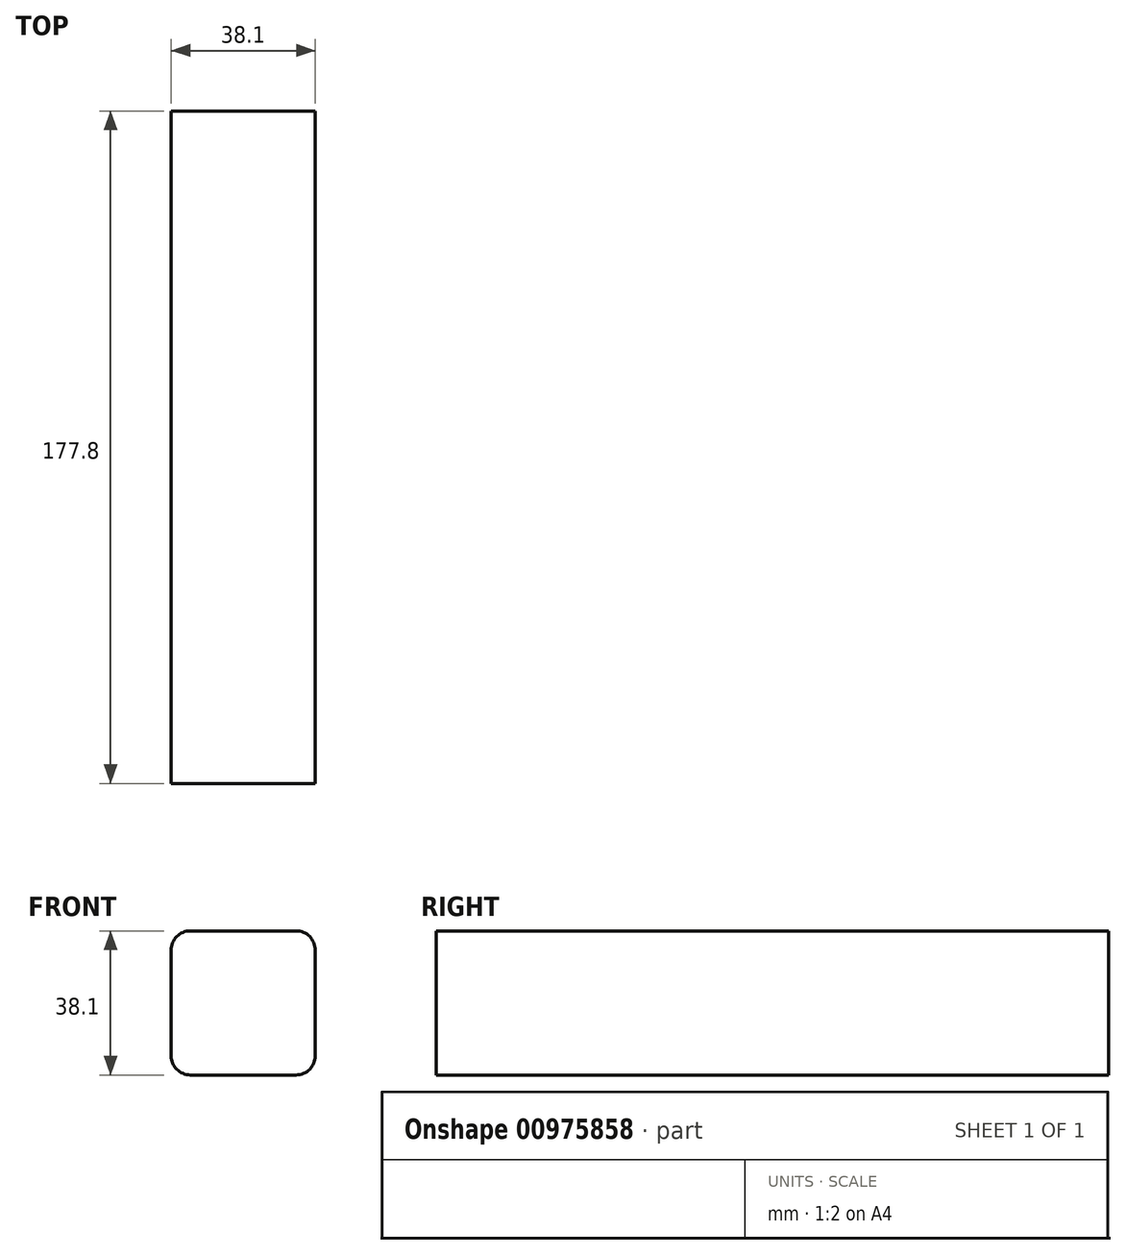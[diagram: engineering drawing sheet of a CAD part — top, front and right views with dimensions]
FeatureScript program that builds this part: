
annotation { "Feature Type Name" : "Feature", "Feature Type Description" : "" }
export const myFeature = defineFeature(function(context is Context, id is Id, definition is map)
    precondition{}
    {
        {
            var Q0;
            Q0=qCreatedBy(makeId("Front.planeOp"),FACE);
            var sketch = newSketch(context, id + "F0", { "sketchPlane" : qUnion([Q0])});
            skLineSegment(sketch, "E0.bottom", {"start": v(0, 0) * mm, "end": v(38.1, 0) * mm});
            skLineSegment(sketch, "E0.top", {"start": v(0, 38.1) * mm, "end": v(38.1, 38.1) * mm});
            skLineSegment(sketch, "E0.left", {"start": v(0, 0) * mm, "end": v(0, 38.1) * mm});
            skLineSegment(sketch, "E0.right", {"start": v(38.1, 0) * mm, "end": v(38.1, 38.1) * mm});
            skSolve(sketch);
        }
        {
            var Q0;
            Q0=makeQuery(id+"F0.imprint","IMPRINT",FACE,{"disambiguationData":[TD([[makeQuery(id+"F0.imprint","IMPRINT",EDGE,{"derivedFrom":sQuery(id+"F0.wireOp",EDGE,"E0.bottom")}),1.0]])]});
            extrude(context, id + "F1", {"entities" : qUnion([Q0]), "depth" : 177.8 * mm, "offsetDistance" : 25.4 * mm});
        }
        {
            var Q0;
            Q0=makeQuery(id+"F1.opExtrude","SWEPT_EDGE",EDGE,{"disambiguationData":[OSD([sQuery(id+"F0.wireOp",EDGE,"E0.top"),sQuery(id+"F0.wireOp",EDGE,"E0.right")])]});
            var Q1;
            Q1=makeQuery(id+"F1.opExtrude","SWEPT_EDGE",EDGE,{"disambiguationData":[OSD([sQuery(id+"F0.wireOp",EDGE,"E0.top"),sQuery(id+"F0.wireOp",EDGE,"E0.left")])]});
            var Q2;
            Q2=makeQuery(id+"F1.opExtrude","SWEPT_EDGE",EDGE,{"disambiguationData":[OSD([sQuery(id+"F0.wireOp",EDGE,"E0.bottom"),sQuery(id+"F0.wireOp",EDGE,"E0.left")])]});
            var Q3;
            Q3=makeQuery(id+"F1.opExtrude","SWEPT_EDGE",EDGE,{"disambiguationData":[OSD([sQuery(id+"F0.wireOp",EDGE,"E0.bottom"),sQuery(id+"F0.wireOp",EDGE,"E0.right")])]});
            fillet(context, id + "F2", {"entities" : qUnion([Q0, Q1, Q2, Q3]), "radius" : 5.08 * mm, "tangentPropagation" : true, "allowEdgeOverflow" : false});
        }
    });
